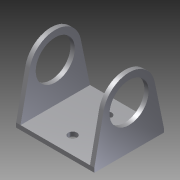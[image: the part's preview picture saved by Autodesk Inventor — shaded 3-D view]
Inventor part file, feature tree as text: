
AUTODESK INVENTOR PART (.ipt)
format: ipt  version: 2012 (Build 160160000, 160)  size: 128,512 bytes
history: native  units: in
note: dims shown in document units (in); Inventor stores cm internally (conversion verified against a paired STEP export)
features: extrude x3, sketch x3
ambient origin geometry x8: Origin, YZ Plane, XZ Plane, XY Plane, X Axis, Y Axis, Z Axis, Center Point
bodies: Solid1 (feature_tree)
feature tree (6):
  extrude  "Extrusion1"  Depth=2.25in
  extrude  "Extrusion2"  Depth=0.125in
  extrude  "Extrusion3"  Depth=2.0in TaperAngle=0.0deg
  sketch  "Sketch1"  dims[d0=2.0in d1=2.25in]
  sketch  "Sketch2"  dims[d2=0.125in d3=0.125in]
  sketch  "Sketch3"  dims[d4=0.125in d5=2.0in d6=0.0in d7=1.125in d8=1.0in d9=0.75in d10=2.0in d11=0.0in d12=0.25in d13=0.25in d14=0.5in d15=1.0in d16=0.5in d17=1.0in d18=2.0in d19=0.0in d20=2.0in]
